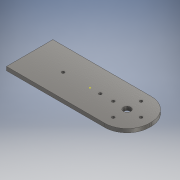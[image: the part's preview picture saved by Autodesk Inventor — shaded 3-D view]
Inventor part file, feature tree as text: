
AUTODESK INVENTOR PART (.ipt)
format: ipt  version: 2018 (Build 220112000, 112)  size: 126,464 bytes
history: native  units: mm
features: fillet x2, sketch x2, other x1, extrude x1
ambient origin geometry x8: Origin, YZ Plane, XZ Plane, XY Plane, X Axis, Y Axis, Z Axis, Center Point
bodies: Body1 (feature_tree)
feature tree (6):
  other  "Sólido1"
  extrude  "Extrusión1"  Depth=25.0mm
  fillet  "Empalme1"  Radius=1.5mm
  fillet  "Empalme2"  Radius=1.5mm
  sketch  "Boceto2"  dims[d13=1.5mm d14=4.0mm d15=1.5mm d16=1.5mm d17=1.5mm d18=2.0mm d19=0.0mm d20=12.0mm d21=12.0mm]
  sketch  "Boceto1"  dims[d0=65.0mm d1=25.0mm d11=1.5mm d12=1.5mm]
